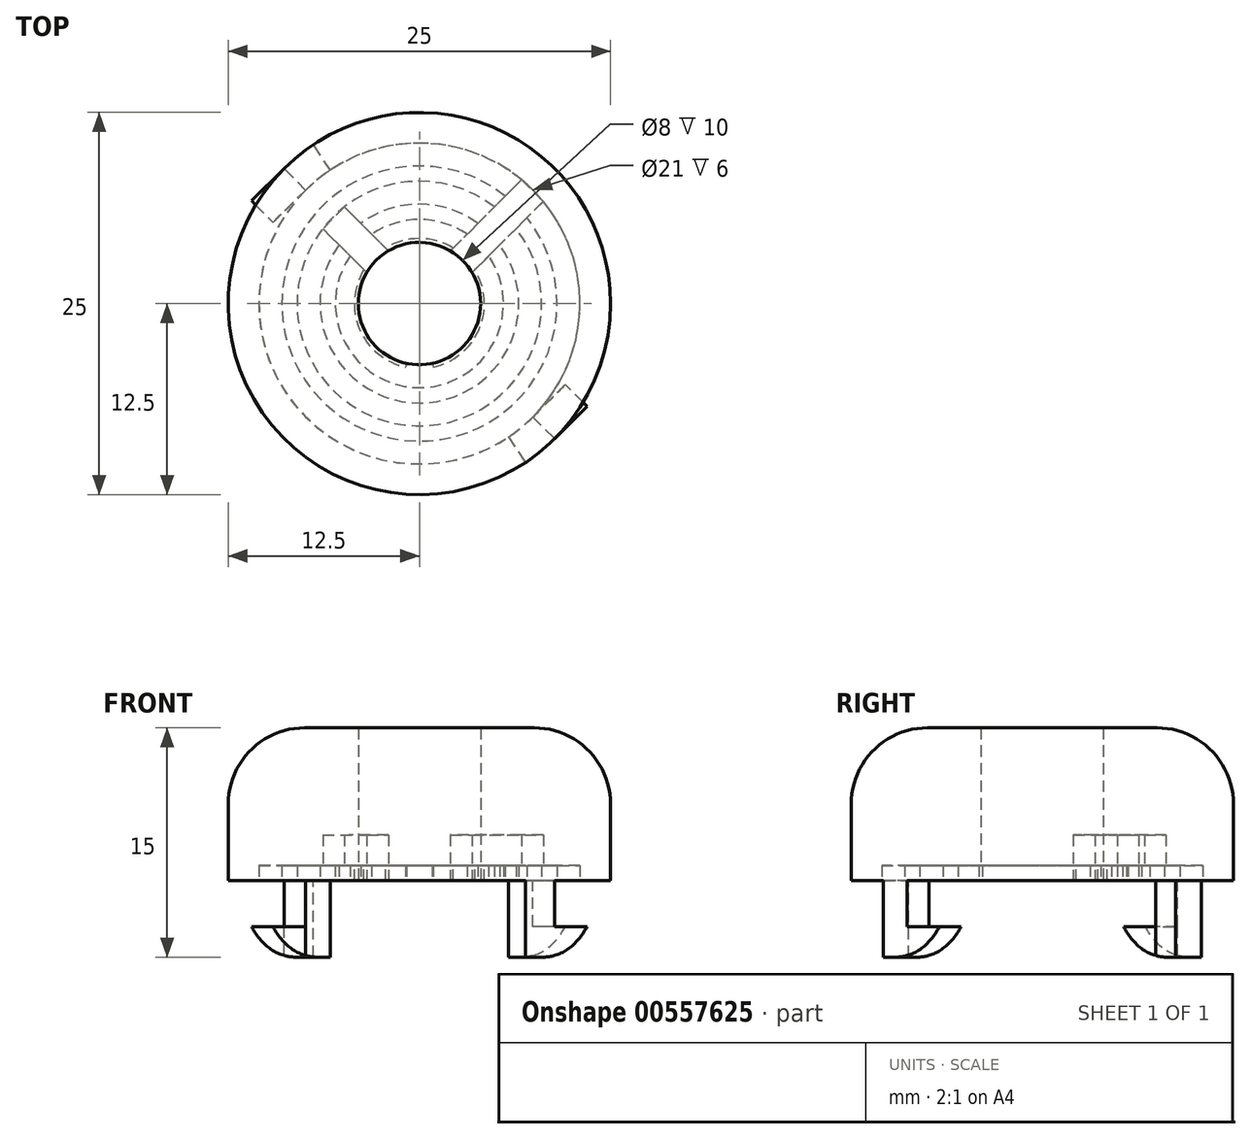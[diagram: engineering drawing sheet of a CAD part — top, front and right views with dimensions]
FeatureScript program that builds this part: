
annotation { "Feature Type Name" : "Feature", "Feature Type Description" : "" }
export const myFeature = defineFeature(function(context is Context, id is Id, definition is map)
    precondition{}
    {
        {
            var Q0;
            Q0=qCreatedBy(makeId("Top.planeOp"),FACE);
            var sketch = newSketch(context, id + "F0", { "sketchPlane" : qUnion([Q0])});
            skCircle(sketch, "E0", {"center": v(0, 0) * mm, "radius": 4 * mm});
            skCircle(sketch, "E1", {"center": v(0, 0) * mm, "radius": 5.5 * mm});
            skCircle(sketch, "E2", {"center": v(0, 0) * mm, "radius": 6.5 * mm});
            skCircle(sketch, "E3", {"center": v(0, 0) * mm, "radius": 8 * mm});
            skCircle(sketch, "E4", {"center": v(0, 0) * mm, "radius": 9 * mm});
            skCircle(sketch, "E5", {"center": v(0, 0) * mm, "radius": 10.5 * mm});
            skCircle(sketch, "E6", {"center": v(0, 0) * mm, "radius": 12.5 * mm});
            skLineSegment(sketch, "E7", {"start": v(-8.84, -8.84) * mm, "end": v(-7.42, -7.42) * mm});
            skLineSegment(sketch, "E8", {"start": v(-7.44, 7.41) * mm, "end": v(-8.84, 8.84) * mm});
            skLineSegment(sketch, "E9", {"start": v(7.42, 7.42) * mm, "end": v(8.84, 8.84) * mm});
            skLineSegment(sketch, "E10", {"start": v(7.42, -7.42) * mm, "end": v(8.84, -8.84) * mm});
            skLineSegment(sketch, "E11", {"start": v(0, 10.5) * mm, "end": v(0, 12.5) * mm});
            skLineSegment(sketch, "E12", {"start": v(-4.02, 9.7) * mm, "end": v(-4.78, 11.55) * mm});
            skLineSegment(sketch, "E13", {"start": v(4.02, -9.7) * mm, "end": v(4.78, -11.55) * mm});
            skLineSegment(sketch, "E14", {"start": v(4.02, 9.7) * mm, "end": v(4.78, 11.55) * mm});
            skLineSegment(sketch, "E15", {"start": v(-4, -9.66) * mm, "end": v(-4.78, -11.55) * mm});
            skLineSegment(sketch, "E16", {"start": v(-5.83, 8.72) * mm, "end": v(-6.94, 10.4) * mm});
            skLineSegment(sketch, "E17", {"start": v(5.83, -8.73) * mm, "end": v(6.94, -10.4) * mm});
            skSolve(sketch);
        }
        {
            var Q0;
            {var subQ0=sQuery(id+"F0.wireOp",EDGE,"E8");Q0=makeQuery(id+"F0.imprint","IMPRINT",FACE,{"disambiguationData":[TD([[makeQuery(id+"F0.imprint","IMPRINT",EDGE,{"derivedFrom":subQ0}),-1.0]])]});}
            var Q1;
            {var subQ0=sQuery(id+"F0.wireOp",EDGE,"E12");Q1=makeQuery(id+"F0.imprint","IMPRINT",FACE,{"disambiguationData":[TD([[makeQuery(id+"F0.imprint","IMPRINT",EDGE,{"derivedFrom":subQ0}),1.0]])]});}
            var Q2;
            {var subQ0=sQuery(id+"F0.wireOp",EDGE,"E11");Q2=makeQuery(id+"F0.imprint","IMPRINT",FACE,{"disambiguationData":[TD([[makeQuery(id+"F0.imprint","IMPRINT",EDGE,{"derivedFrom":subQ0}),1.0]])]});}
            var Q3;
            {var subQ0=sQuery(id+"F0.wireOp",EDGE,"E11");Q3=makeQuery(id+"F0.imprint","IMPRINT",FACE,{"disambiguationData":[TD([[makeQuery(id+"F0.imprint","IMPRINT",EDGE,{"derivedFrom":subQ0}),-1.0]])]});}
            var Q4;
            {var subQ0=sQuery(id+"F0.wireOp",EDGE,"E9");Q4=makeQuery(id+"F0.imprint","IMPRINT",FACE,{"disambiguationData":[TD([[makeQuery(id+"F0.imprint","IMPRINT",EDGE,{"derivedFrom":subQ0}),1.0]])]});}
            var Q5;
            Q5=makeQuery(id+"F0.imprint","IMPRINT",FACE,{"disambiguationData":[TD([[makeQuery(id+"F0.imprint","IMPRINT",EDGE,{"derivedFrom":sQuery(id+"F0.wireOp",EDGE,"E4")}),-1.0]])]});
            var Q6;
            {var subQ0=sQuery(id+"F0.wireOp",EDGE,"E9");Q6=makeQuery(id+"F0.imprint","IMPRINT",FACE,{"disambiguationData":[TD([[makeQuery(id+"F0.imprint","IMPRINT",EDGE,{"derivedFrom":subQ0}),-1.0]])]});}
            var Q7;
            {var subQ0=sQuery(id+"F0.wireOp",EDGE,"E13");Q7=makeQuery(id+"F0.imprint","IMPRINT",FACE,{"disambiguationData":[TD([[makeQuery(id+"F0.imprint","IMPRINT",EDGE,{"derivedFrom":subQ0}),1.0]])]});}
            var Q8;
            {var subQ0=sQuery(id+"F0.wireOp",EDGE,"E7");Q8=makeQuery(id+"F0.imprint","IMPRINT",FACE,{"disambiguationData":[TD([[makeQuery(id+"F0.imprint","IMPRINT",EDGE,{"derivedFrom":subQ0}),1.0]])]});}
            var Q9;
            Q9=makeQuery(id+"F0.imprint","IMPRINT",FACE,{"disambiguationData":[TD([[makeQuery(id+"F0.imprint","IMPRINT",EDGE,{"derivedFrom":sQuery(id+"F0.wireOp",EDGE,"E3")}),-1.0]])]});
            var Q10;
            {var subQ0=sQuery(id+"F0.wireOp",EDGE,"E7");Q10=makeQuery(id+"F0.imprint","IMPRINT",FACE,{"disambiguationData":[TD([[makeQuery(id+"F0.imprint","IMPRINT",EDGE,{"derivedFrom":subQ0}),-1.0]])]});}
            var Q11;
            Q11=makeQuery(id+"F0.imprint","IMPRINT",FACE,{"disambiguationData":[TD([[makeQuery(id+"F0.imprint","IMPRINT",EDGE,{"derivedFrom":sQuery(id+"F0.wireOp",EDGE,"E1")}),-1.0]])]});
            var Q12;
            {var subQ0=sQuery(id+"F0.wireOp",EDGE,"E10");Q12=makeQuery(id+"F0.imprint","IMPRINT",FACE,{"disambiguationData":[TD([[makeQuery(id+"F0.imprint","IMPRINT",EDGE,{"derivedFrom":subQ0}),-1.0]])]});}
            var Q13;
            Q13=makeQuery(id+"F0.imprint","IMPRINT",FACE,{"disambiguationData":[TD([[makeQuery(id+"F0.imprint","IMPRINT",EDGE,{"derivedFrom":sQuery(id+"F0.wireOp",EDGE,"E0")}),1.0]])]});
            var Q14;
            Q14=makeQuery(id+"F0.imprint","IMPRINT",FACE,{"disambiguationData":[TD([[makeQuery(id+"F0.imprint","IMPRINT",EDGE,{"derivedFrom":sQuery(id+"F0.wireOp",EDGE,"E0")}),-1.0]])]});
            var Q15;
            {var subQ0=sQuery(id+"F0.wireOp",EDGE,"E13");Q15=makeQuery(id+"F0.imprint","IMPRINT",FACE,{"disambiguationData":[TD([[makeQuery(id+"F0.imprint","IMPRINT",EDGE,{"derivedFrom":subQ0}),-1.0]])]});}
            var Q16;
            Q16=makeQuery(id+"F0.imprint","IMPRINT",FACE,{"disambiguationData":[TD([[makeQuery(id+"F0.imprint","IMPRINT",EDGE,{"derivedFrom":sQuery(id+"F0.wireOp",EDGE,"E2")}),-1.0]])]});
            extrude(context, id + "F1", {"entities" : qUnion([Q0, Q1, Q2, Q3, Q4, Q5, Q6, Q7, Q8, Q9, Q10, Q11, Q12, Q13, Q14, Q15, Q16]), "depth" : 10 * mm, "offsetDistance" : 25 * mm});
        }
        {
            var Q0;
            Q0=makeQuery(id+"F0.imprint","IMPRINT",FACE,{"disambiguationData":[TD([[makeQuery(id+"F0.imprint","IMPRINT",EDGE,{"derivedFrom":sQuery(id+"F0.wireOp",EDGE,"E4")}),-1.0]])]});
            var Q1;
            Q1=makeQuery(id+"F0.imprint","IMPRINT",FACE,{"disambiguationData":[TD([[makeQuery(id+"F0.imprint","IMPRINT",EDGE,{"derivedFrom":sQuery(id+"F0.wireOp",EDGE,"E2")}),-1.0]])]});
            var Q2;
            Q2=makeQuery(id+"F0.imprint","IMPRINT",FACE,{"disambiguationData":[TD([[makeQuery(id+"F0.imprint","IMPRINT",EDGE,{"derivedFrom":sQuery(id+"F0.wireOp",EDGE,"E0")}),-1.0]])]});
            extrude(context, id + "F2", {"entities" : qUnion([Q0, Q1, Q2]), "operationType" : NewBodyOperationType.REMOVE, "depth" : 1 * mm, "offsetDistance" : 25 * mm});
        }
        {
            var Q0;
            {var subQ0=sQuery(id+"F0.wireOp",EDGE,"E9");Q0=makeQuery(id+"F0.imprint","IMPRINT",FACE,{"disambiguationData":[TD([[makeQuery(id+"F0.imprint","IMPRINT",EDGE,{"derivedFrom":subQ0}),1.0]])]});}
            var Q1;
            {var subQ0=sQuery(id+"F0.wireOp",EDGE,"E7");Q1=makeQuery(id+"F0.imprint","IMPRINT",FACE,{"disambiguationData":[TD([[makeQuery(id+"F0.imprint","IMPRINT",EDGE,{"derivedFrom":subQ0}),-1.0]])]});}
            extrude(context, id + "F3", {"entities" : qUnion([Q0, Q1]), "operationType" : NewBodyOperationType.REMOVE, "depth" : 5 * mm, "offsetDistance" : 25 * mm});
        }
        {
            var Q0;
            {var subQ0=sQuery(id+"F0.wireOp",EDGE,"E8");Q0=makeQuery(id+"F0.imprint","IMPRINT",FACE,{"disambiguationData":[TD([[makeQuery(id+"F0.imprint","IMPRINT",EDGE,{"derivedFrom":subQ0}),-1.0]])]});}
            var Q1;
            {var subQ0=sQuery(id+"F0.wireOp",EDGE,"E10");Q1=makeQuery(id+"F0.imprint","IMPRINT",FACE,{"disambiguationData":[TD([[makeQuery(id+"F0.imprint","IMPRINT",EDGE,{"derivedFrom":subQ0}),-1.0]])]});}
            extrude(context, id + "F4", {"entities" : qUnion([Q0, Q1]), "operationType" : NewBodyOperationType.ADD, "oppositeDirection" : true, "depth" : 5 * mm, "offsetDistance" : 25 * mm});
        }
        {
            var Q0;
            Q0=makeQuery(id+"F4.opExtrude","SWEPT_FACE",FACE,{"disambiguationData":[OSD([sQuery(id+"F0.wireOp",EDGE,"E8")])]});
            var sketch = newSketch(context, id + "F5", { "sketchPlane" : qUnion([Q0])});
            skLineSegment(sketch, "E18", {"start": v(-12.5, -5) * mm, "end": v(-12.5, -3) * mm});
            skLineSegment(sketch, "E19", {"start": v(-12.5, -3) * mm, "end": v(-10.5, -3) * mm});
            skLineSegment(sketch, "E20", {"start": v(-10.5, -3) * mm, "end": v(-10.5, -5) * mm});
            skLineSegment(sketch, "E21", {"start": v(-10.5, -5) * mm, "end": v(-12.5, -5) * mm});
            skSolve(sketch);
        }
        {
            var Q0;
            Q0=makeQuery(id+"F5.imprint","IMPRINT",FACE,{"disambiguationData":[TD([[makeQuery(id+"F5.imprint","IMPRINT",EDGE,{"derivedFrom":sQuery(id+"F5.wireOp",EDGE,"E18")}),-1.0]])]});
            extrude(context, id + "F6", {"entities" : qUnion([Q0]), "operationType" : NewBodyOperationType.ADD, "depth" : 3 * mm, "offsetDistance" : 25 * mm});
        }
        {
            var Q0;
            Q0=makeQuery(id+"F4.opExtrude","SWEPT_FACE",FACE,{"disambiguationData":[OSD([sQuery(id+"F0.wireOp",EDGE,"E10")])]});
            var sketch = newSketch(context, id + "F7", { "sketchPlane" : qUnion([Q0])});
            skLineSegment(sketch, "E22", {"start": v(-12.5, -5) * mm, "end": v(-12.5, -3) * mm});
            skLineSegment(sketch, "E23", {"start": v(-12.5, -3) * mm, "end": v(-10.5, -3) * mm});
            skLineSegment(sketch, "E24", {"start": v(-10.5, -3) * mm, "end": v(-10.5, -5) * mm});
            skLineSegment(sketch, "E25", {"start": v(-10.5, -5) * mm, "end": v(-12.5, -5) * mm});
            skSolve(sketch);
        }
        {
            var Q0;
            Q0=makeQuery(id+"F7.imprint","IMPRINT",FACE,{"disambiguationData":[TD([[makeQuery(id+"F7.imprint","IMPRINT",EDGE,{"derivedFrom":sQuery(id+"F7.wireOp",EDGE,"E22")}),-1.0]])]});
            extrude(context, id + "F8", {"entities" : qUnion([Q0]), "operationType" : NewBodyOperationType.ADD, "depth" : 3 * mm, "offsetDistance" : 25 * mm});
        }
        {
            var Q0;
            Q0=makeQuery(id+"F3.boolean.opBoolean","COPY",FACE,{"derivedFrom":makeQuery(id+"F3.opExtrude","SWEPT_FACE",FACE,{"disambiguationData":[OSD([sQuery(id+"F0.wireOp",EDGE,"E14")])]})});
            var sketch = newSketch(context, id + "F9", { "sketchPlane" : qUnion([Q0])});
            skLineSegment(sketch, "E26", {"start": v(10.5, 1) * mm, "end": v(12.5, 1) * mm});
            skLineSegment(sketch, "E27", {"start": v(12.5, 1) * mm, "end": v(12.5, 5) * mm});
            skLineSegment(sketch, "E28", {"start": v(12.5, 5) * mm, "end": v(10.5, 5) * mm});
            skLineSegment(sketch, "E29", {"start": v(10.5, 5) * mm, "end": v(10.5, 1) * mm});
            skSolve(sketch);
        }
        {
            var Q0;
            Q0=makeQuery(id+"F9.imprint","IMPRINT",FACE,{"disambiguationData":[TD([[makeQuery(id+"F9.imprint","IMPRINT",EDGE,{"derivedFrom":sQuery(id+"F9.wireOp",EDGE,"E26")}),1.0]])]});
            extrude(context, id + "F10", {"entities" : qUnion([Q0]), "operationType" : NewBodyOperationType.REMOVE, "oppositeDirection" : true, "depth" : 5 * mm, "offsetDistance" : 25 * mm});
        }
        {
            var Q0;
            Q0=makeQuery(id+"F3.boolean.opBoolean","COPY",FACE,{"derivedFrom":makeQuery(id+"F3.opExtrude","SWEPT_FACE",FACE,{"disambiguationData":[OSD([sQuery(id+"F0.wireOp",EDGE,"E7")])]})});
            var sketch = newSketch(context, id + "F11", { "sketchPlane" : qUnion([Q0])});
            skLineSegment(sketch, "E30", {"start": v(-10.5, 1) * mm, "end": v(-12.5, 1) * mm});
            skLineSegment(sketch, "E31", {"start": v(-12.5, 1) * mm, "end": v(-12.5, 5) * mm});
            skLineSegment(sketch, "E32", {"start": v(-12.5, 5) * mm, "end": v(-10.5, 5) * mm});
            skLineSegment(sketch, "E33", {"start": v(-10.5, 5) * mm, "end": v(-10.5, 1) * mm});
            skSolve(sketch);
        }
        {
            var Q0;
            Q0=makeQuery(id+"F11.imprint","IMPRINT",FACE,{"disambiguationData":[TD([[makeQuery(id+"F11.imprint","IMPRINT",EDGE,{"derivedFrom":sQuery(id+"F11.wireOp",EDGE,"E30")}),-1.0]])]});
            extrude(context, id + "F12", {"entities" : qUnion([Q0]), "operationType" : NewBodyOperationType.REMOVE, "oppositeDirection" : true, "depth" : 5 * mm, "offsetDistance" : 25 * mm});
        }
        {
            var Q0;
            Q0=makeQuery(id+"F3.boolean.opBoolean","COPY",FACE,{"derivedFrom":makeQuery(id+"F3.opExtrude","SWEPT_FACE",FACE,{"disambiguationData":[OSD([sQuery(id+"F0.wireOp",EDGE,"E15")])]})});
            var sketch = newSketch(context, id + "F13", { "sketchPlane" : qUnion([Q0])});
            skLineSegment(sketch, "E34", {"start": v(10.5, 1) * mm, "end": v(12.5, 1) * mm});
            skLineSegment(sketch, "E35", {"start": v(12.5, 1) * mm, "end": v(12.5, 5) * mm});
            skLineSegment(sketch, "E36", {"start": v(12.5, 5) * mm, "end": v(10.5, 5) * mm});
            skLineSegment(sketch, "E37", {"start": v(10.5, 5) * mm, "end": v(10.5, 1) * mm});
            skSolve(sketch);
        }
        {
            var Q0;
            Q0=makeQuery(id+"F13.imprint","IMPRINT",FACE,{"disambiguationData":[TD([[makeQuery(id+"F13.imprint","IMPRINT",EDGE,{"derivedFrom":sQuery(id+"F13.wireOp",EDGE,"E34")}),1.0]])]});
            extrude(context, id + "F14", {"entities" : qUnion([Q0]), "operationType" : NewBodyOperationType.REMOVE, "oppositeDirection" : true, "depth" : 5 * mm, "offsetDistance" : 25 * mm});
        }
        {
            var Q0;
            Q0=makeQuery(id+"F3.boolean.opBoolean","COPY",FACE,{"derivedFrom":makeQuery(id+"F3.opExtrude","SWEPT_FACE",FACE,{"disambiguationData":[OSD([sQuery(id+"F0.wireOp",EDGE,"E9")])]})});
            var sketch = newSketch(context, id + "F15", { "sketchPlane" : qUnion([Q0])});
            skLineSegment(sketch, "E38", {"start": v(-10.5, 1) * mm, "end": v(-12.5, 1) * mm});
            skPoint(sketch, "E38.endSnap0", {"position": v(-12.5, 2.5) * mm});
            skLineSegment(sketch, "E39", {"start": v(-12.5, 1) * mm, "end": v(-12.5, 5) * mm});
            skLineSegment(sketch, "E40", {"start": v(-12.5, 5) * mm, "end": v(-10.5, 5) * mm});
            skLineSegment(sketch, "E41", {"start": v(-10.5, 5) * mm, "end": v(-10.5, 1) * mm});
            skSolve(sketch);
        }
        {
            var Q0;
            Q0=makeQuery(id+"F15.imprint","IMPRINT",FACE,{"disambiguationData":[TD([[makeQuery(id+"F15.imprint","IMPRINT",EDGE,{"derivedFrom":sQuery(id+"F15.wireOp",EDGE,"E38")}),-1.0]])]});
            extrude(context, id + "F16", {"entities" : qUnion([Q0]), "operationType" : NewBodyOperationType.REMOVE, "oppositeDirection" : true, "depth" : 5 * mm, "offsetDistance" : 25 * mm});
        }
        {
            var Q0;
            Q0=makeQuery(id+"F8.opExtrude","CAP_EDGE",EDGE,{"disambiguationData":[OSD([sQuery(id+"F7.wireOp",EDGE,"E25")])],"isStart":false});
            fillet(context, id + "F17", {"entities" : qUnion([Q0]), "radius" : 5 * mm, "tangentPropagation" : true, "allowEdgeOverflow" : false});
        }
        {
            var Q0;
            Q0=makeQuery(id+"F6.opExtrude","CAP_EDGE",EDGE,{"disambiguationData":[OSD([sQuery(id+"F5.wireOp",EDGE,"E21")])],"isStart":false});
            fillet(context, id + "F18", {"entities" : qUnion([Q0]), "radius" : 5 * mm, "tangentPropagation" : true, "allowEdgeOverflow" : false});
        }
        {
            var Q0;
            Q0=makeQuery(id+"F0.imprint","IMPRINT",FACE,{"disambiguationData":[TD([[makeQuery(id+"F0.imprint","IMPRINT",EDGE,{"derivedFrom":sQuery(id+"F0.wireOp",EDGE,"E0")}),1.0]])]});
            extrude(context, id + "F19", {"entities" : qUnion([Q0]), "operationType" : NewBodyOperationType.REMOVE, "depth" : 25 * mm, "offsetDistance" : 25 * mm});
        }
        {
            var Q0;
            Q0=makeQuery(id+"F1.opExtrude","CAP_EDGE",EDGE,{"disambiguationData":[OSD([sQuery(id+"F0.wireOp",EDGE,"E6")])],"isStart":false});
            fillet(context, id + "F20", {"entities" : qUnion([Q0]), "radius" : 5 * mm, "tangentPropagation" : true, "allowEdgeOverflow" : false});
        }
        {
            var Q0;
            Q0=makeQuery(id+"F14.boolean.opBoolean","MERGE",FACE,{"derivedFrom":[makeQuery(id+"F12.boolean.opBoolean","MERGE",FACE,{"derivedFrom":[makeQuery(id+"F3.boolean.opBoolean","COPY",FACE,{"derivedFrom":makeQuery(id+"F3.opExtrude","CAP_FACE",FACE,{"disambiguationData":[OSD([sQuery(id+"F0.wireOp",EDGE,"E5"),sQuery(id+"F0.wireOp",EDGE,"E6"),sQuery(id+"F0.wireOp",EDGE,"E7"),sQuery(id+"F0.wireOp",EDGE,"E15")])],"isStart":false})}),makeQuery(id+"F12.opExtrude","SWEPT_FACE",FACE,{"disambiguationData":[OSD([sQuery(id+"F11.wireOp",EDGE,"E32")])]})]}),makeQuery(id+"F14.opExtrude","SWEPT_FACE",FACE,{"disambiguationData":[OSD([sQuery(id+"F13.wireOp",EDGE,"E36")])]})]});
            extrude(context, id + "F21", {"entities" : qUnion([Q0]), "operationType" : NewBodyOperationType.ADD, "depth" : 5 * mm, "offsetDistance" : 25 * mm});
        }
        {
            var Q0;
            Q0=makeQuery(id+"F16.boolean.opBoolean","MERGE",FACE,{"derivedFrom":[makeQuery(id+"F10.boolean.opBoolean","MERGE",FACE,{"derivedFrom":[makeQuery(id+"F3.boolean.opBoolean","COPY",FACE,{"derivedFrom":makeQuery(id+"F3.opExtrude","CAP_FACE",FACE,{"disambiguationData":[OSD([sQuery(id+"F0.wireOp",EDGE,"E5"),sQuery(id+"F0.wireOp",EDGE,"E6"),sQuery(id+"F0.wireOp",EDGE,"E9"),sQuery(id+"F0.wireOp",EDGE,"E14")])],"isStart":false})}),makeQuery(id+"F10.opExtrude","SWEPT_FACE",FACE,{"disambiguationData":[OSD([sQuery(id+"F9.wireOp",EDGE,"E28")])]})]}),makeQuery(id+"F16.opExtrude","SWEPT_FACE",FACE,{"disambiguationData":[OSD([sQuery(id+"F15.wireOp",EDGE,"E40")])]})]});
            extrude(context, id + "F22", {"entities" : qUnion([Q0]), "operationType" : NewBodyOperationType.ADD, "depth" : 5 * mm, "offsetDistance" : 25 * mm});
        }
        {
            var Q0;
            Q0=makeQuery(id+"F2.boolean.opBoolean","COPY",FACE,{"derivedFrom":makeQuery(id+"F2.opExtrude","CAP_FACE",FACE,{"disambiguationData":[OSD([sQuery(id+"F0.wireOp",EDGE,"E0"),sQuery(id+"F0.wireOp",EDGE,"E1")])],"isStart":false})});
            var sketch = newSketch(context, id + "F23", { "sketchPlane" : qUnion([Q0])});
            skCircle(sketch, "E42", {"center": v(0, 0) * mm, "radius": 4.25 * mm});
            skSolve(sketch);
        }
        {
            var Q0;
            Q0=makeQuery(id+"F23.imprint","IMPRINT",FACE,{"disambiguationData":[TD([[makeQuery(id+"F23.imprint","IMPRINT",EDGE,{"derivedFrom":sQuery(id+"F23.wireOp",EDGE,"E42")}),1.0]])]});
            extrude(context, id + "F24", {"entities" : qUnion([Q0]), "operationType" : NewBodyOperationType.ADD, "depth" : 1 * mm, "offsetDistance" : 25 * mm});
        }
        {
            var Q0;
            Q0=makeQuery(id+"F24.opExtrude","CAP_FACE",FACE,{"disambiguationData":[OSD([sQuery(id+"F0.wireOp",EDGE,"E0"),sQuery(id+"F23.wireOp",EDGE,"E42")])],"isStart":false});
            var sketch = newSketch(context, id + "F25", { "sketchPlane" : qUnion([Q0])});
            skLineSegment(sketch, "E43", {"start": v(0, 0) * mm, "end": v(0.9, 4.15) * mm});
            skLineSegment(sketch, "E44", {"start": v(0, 0) * mm, "end": v(-0.9, 4.15) * mm});
            skSolve(sketch);
        }
        {
            var Q0;
            {var subQ0=sQuery(id+"F25.wireOp",EDGE,"E43");var subQ1=makeQuery(id+"F24.opExtrude","CAP_EDGE",EDGE,{"disambiguationData":[OSD([sQuery(id+"F23.wireOp",EDGE,"E42")])],"isStart":false});var subQ2=makeQuery(id+"F25.imprint","INTERSECT",VERTEX,{"derivedFrom":[subQ1,subQ0]});Q0=makeQuery(id+"F25.imprint","IMPRINT",FACE,{"disambiguationData":[TD([[makeQuery(id+"F25.imprint","IMPRINT",EDGE,{"disambiguationData":[TD([[subQ2,1.0]])],"derivedFrom":subQ0}),1.0]])]});}
            extrude(context, id + "F26", {"entities" : qUnion([Q0]), "operationType" : NewBodyOperationType.REMOVE, "oppositeDirection" : true, "depth" : 1 * mm, "offsetDistance" : 25 * mm});
        }
        {
            var Q0;
            Q0=makeQuery(id+"F2.boolean.opBoolean","SPLIT",FACE,{"disambiguationData":[TD([makeQuery(id+"F2.opExtrude","SWEPT_FACE",FACE,{"disambiguationData":[OSD([sQuery(id+"F0.wireOp",EDGE,"E1")])]})])],"derivedFrom":makeQuery(id+"F1.opExtrude","CAP_FACE",FACE,{"disambiguationData":[OSD([sQuery(id+"F0.wireOp",EDGE,"E6")])],"isStart":true})});
            var sketch = newSketch(context, id + "F27", { "sketchPlane" : qUnion([Q0])});
            skLineSegment(sketch, "E45", {"start": v(0, 0) * mm, "end": v(-5.61, -5.61) * mm});
            skLineSegment(sketch, "E46", {"start": v(-2.14, -2.14) * mm, "end": v(-1.44, -2.85) * mm});
            skLineSegment(sketch, "E47", {"start": v(-1.44, -2.85) * mm, "end": v(-4.6, -6.02) * mm});
            skLineSegment(sketch, "E48", {"start": v(-4.6, -6.02) * mm, "end": v(-6.02, -4.6) * mm});
            skLineSegment(sketch, "E49", {"start": v(-6.02, -4.6) * mm, "end": v(-2.83, -1.42) * mm});
            skLineSegment(sketch, "E50", {"start": v(-2.83, -1.42) * mm, "end": v(-2.14, -2.14) * mm});
            skLineSegment(sketch, "E51", {"start": v(-6.02, -4.6) * mm, "end": v(-6.31, -4.9) * mm});
            skLineSegment(sketch, "E52", {"start": v(-6.31, -4.9) * mm, "end": v(-4.9, -6.31) * mm});
            skLineSegment(sketch, "E53", {"start": v(-4.9, -6.31) * mm, "end": v(-4.6, -6.02) * mm});
            skSolve(sketch);
        }
        {
            var Q0;
            {var subQ0=sQuery(id+"F27.wireOp",EDGE,"E48");var subQ1=sQuery(id+"F27.wireOp",EDGE,"E45");var subQ2=makeQuery(id+"F27.imprint","INTERSECT",VERTEX,{"derivedFrom":[subQ1,subQ0]});Q0=makeQuery(id+"F27.imprint","IMPRINT",FACE,{"disambiguationData":[TD([[makeQuery(id+"F27.imprint","IMPRINT",EDGE,{"disambiguationData":[TD([[subQ2,1.0]])],"derivedFrom":subQ1}),-1.0]])]});}
            var Q1;
            {var subQ0=sQuery(id+"F27.wireOp",EDGE,"E48");var subQ1=sQuery(id+"F27.wireOp",EDGE,"E45");var subQ2=makeQuery(id+"F27.imprint","INTERSECT",VERTEX,{"derivedFrom":[subQ1,subQ0]});Q1=makeQuery(id+"F27.imprint","IMPRINT",FACE,{"disambiguationData":[TD([[makeQuery(id+"F27.imprint","IMPRINT",EDGE,{"disambiguationData":[TD([[subQ2,1.0]])],"derivedFrom":subQ1}),1.0]])]});}
            var Q2;
            {var subQ0=sQuery(id+"F27.wireOp",EDGE,"E45");var subQ1=makeQuery(id+"F2.boolean.opBoolean","COPY",EDGE,{"derivedFrom":makeQuery(id+"F2.opExtrude","CAP_EDGE",EDGE,{"disambiguationData":[OSD([sQuery(id+"F0.wireOp",EDGE,"E1")])],"isStart":true})});var subQ2=makeQuery(id+"F27.imprint","INTERSECT",VERTEX,{"derivedFrom":[subQ1,subQ0]});Q2=makeQuery(id+"F27.imprint","IMPRINT",FACE,{"disambiguationData":[TD([[makeQuery(id+"F27.imprint","IMPRINT",EDGE,{"disambiguationData":[TD([[subQ2,-1.0]])],"derivedFrom":subQ0}),-1.0]])]});}
            var Q3;
            {var subQ0=sQuery(id+"F27.wireOp",EDGE,"E45");var subQ1=makeQuery(id+"F2.boolean.opBoolean","COPY",EDGE,{"derivedFrom":makeQuery(id+"F2.opExtrude","CAP_EDGE",EDGE,{"disambiguationData":[OSD([sQuery(id+"F0.wireOp",EDGE,"E1")])],"isStart":true})});var subQ2=makeQuery(id+"F27.imprint","INTERSECT",VERTEX,{"derivedFrom":[subQ1,subQ0]});Q3=makeQuery(id+"F27.imprint","IMPRINT",FACE,{"disambiguationData":[TD([[makeQuery(id+"F27.imprint","IMPRINT",EDGE,{"disambiguationData":[TD([[subQ2,-1.0]])],"derivedFrom":subQ0}),1.0]])]});}
            var Q4;
            {var subQ0=sQuery(id+"F27.wireOp",EDGE,"E46");Q4=makeQuery(id+"F27.imprint","IMPRINT",FACE,{"disambiguationData":[TD([[makeQuery(id+"F27.imprint","IMPRINT",EDGE,{"derivedFrom":subQ0}),-1.0]])]});}
            var Q5;
            {var subQ0=sQuery(id+"F27.wireOp",EDGE,"E50");Q5=makeQuery(id+"F27.imprint","IMPRINT",FACE,{"disambiguationData":[TD([[makeQuery(id+"F27.imprint","IMPRINT",EDGE,{"derivedFrom":subQ0}),-1.0]])]});}
            extrude(context, id + "F28", {"entities" : qUnion([Q0, Q1, Q2, Q3, Q4, Q5]), "operationType" : NewBodyOperationType.REMOVE, "oppositeDirection" : true, "depth" : 3 * mm, "offsetDistance" : 25 * mm});
        }
        {
            var Q0;
            {var subQ5=sQuery(id+"F27.wireOp",EDGE,"E51");Q0=makeQuery(id+"F27.imprint","IMPRINT",FACE,{"disambiguationData":[TD([[makeQuery(id+"F27.imprint","IMPRINT",EDGE,{"derivedFrom":subQ5}),1.0]])]});}
            var Q1;
            {var subQ5=sQuery(id+"F27.wireOp",EDGE,"E53");Q1=makeQuery(id+"F27.imprint","IMPRINT",FACE,{"disambiguationData":[TD([[makeQuery(id+"F27.imprint","IMPRINT",EDGE,{"derivedFrom":subQ5}),1.0]])]});}
            extrude(context, id + "F29", {"entities" : qUnion([Q0, Q1]), "operationType" : NewBodyOperationType.REMOVE, "oppositeDirection" : true, "depth" : 3 * mm, "offsetDistance" : 25 * mm});
        }
        {
            var Q0;
            {var subQ0=sQuery(id+"F0.wireOp",EDGE,"E14");var subQ1=sQuery(id+"F0.wireOp",EDGE,"E9");var subQ2=sQuery(id+"F0.wireOp",EDGE,"E6");var subQ3=sQuery(id+"F0.wireOp",EDGE,"E5");var subQ6=makeQuery(id+"F3.opExtrude","SWEPT_FACE",FACE,{"disambiguationData":[OSD([subQ1])]});var subQ10=makeQuery(id+"F1.opExtrude","SWEPT_FACE",FACE,{"disambiguationData":[OSD([subQ2])]});var subQ14=makeQuery(id+"F2.boolean.opBoolean","SPLIT",FACE,{"disambiguationData":[TD([subQ10])],"derivedFrom":makeQuery(id+"F1.opExtrude","CAP_FACE",FACE,{"disambiguationData":[OSD([subQ2])],"isStart":true})});var subQ15=makeQuery(id+"F3.opExtrude","SWEPT_FACE",FACE,{"disambiguationData":[OSD([subQ0])]});Q0=makeQuery(id+"F22.boolean.opBoolean","MERGE",FACE,{"derivedFrom":[makeQuery(id+"F4.boolean.opBoolean","SPLIT",FACE,{"disambiguationData":[TD([makeQuery(id+"F3.boolean.opBoolean","COPY",FACE,{"derivedFrom":subQ15})])],"derivedFrom":makeQuery(id+"F3.boolean.opBoolean","SPLIT",FACE,{"disambiguationData":[TD([makeQuery(id+"F3.opExtrude","SWEPT_FACE",FACE,{"disambiguationData":[OSD([sQuery(id+"F0.wireOp",EDGE,"E7")])]})])],"derivedFrom":subQ14})}),makeQuery(id+"F4.boolean.opBoolean","SPLIT",FACE,{"disambiguationData":[TD([makeQuery(id+"F3.boolean.opBoolean","COPY",FACE,{"derivedFrom":subQ6})])],"derivedFrom":makeQuery(id+"F3.boolean.opBoolean","SPLIT",FACE,{"disambiguationData":[TD([subQ6])],"derivedFrom":subQ14})}),makeQuery(id+"F22.opExtrude","CAP_FACE",FACE,{"disambiguationData":[OSD([subQ3,subQ2,subQ1,subQ0,sQuery(id+"F9.wireOp",EDGE,"E28"),sQuery(id+"F15.wireOp",EDGE,"E40")])],"isStart":false})]});}
            var sketch = newSketch(context, id + "F30", { "sketchPlane" : qUnion([Q0])});
            skLineSegment(sketch, "E54", {"start": v(0, 0) * mm, "end": v(7.42, -7.42) * mm});
            skLineSegment(sketch, "E55", {"start": v(2.02, -2.02) * mm, "end": v(2.72, -1.3) * mm});
            skLineSegment(sketch, "E56", {"start": v(2.72, -1.3) * mm, "end": v(8.1, -6.68) * mm});
            skLineSegment(sketch, "E57", {"start": v(8.1, -6.68) * mm, "end": v(6.68, -8.1) * mm});
            skLineSegment(sketch, "E58", {"start": v(6.68, -8.1) * mm, "end": v(1.3, -2.7) * mm});
            skLineSegment(sketch, "E59", {"start": v(1.3, -2.7) * mm, "end": v(2.02, -2.02) * mm});
            skSolve(sketch);
        }
        {
            var Q0;
            {var subQ0=sQuery(id+"F30.wireOp",EDGE,"E55");Q0=makeQuery(id+"F30.imprint","IMPRINT",FACE,{"disambiguationData":[TD([[makeQuery(id+"F30.imprint","IMPRINT",EDGE,{"derivedFrom":subQ0}),-1.0]])]});}
            var Q1;
            {var subQ4=sQuery(id+"F30.wireOp",EDGE,"E58");Q1=makeQuery(id+"F30.imprint","IMPRINT",FACE,{"disambiguationData":[TD([[makeQuery(id+"F30.imprint","IMPRINT",EDGE,{"derivedFrom":subQ4}),-1.0]])]});}
            extrude(context, id + "F31", {"entities" : qUnion([Q0, Q1]), "operationType" : NewBodyOperationType.REMOVE, "oppositeDirection" : true, "depth" : 3 * mm, "offsetDistance" : 25 * mm});
        }
    });
